# Revit family: Grinder_Pump-Zoeller-840_Series
name_source: partatom
category: Mechanical Equipment
revit_build: Autodesk Revit 2014 (Build: 20130308_1515(x64)
units: mm (PartAtom-declared; Revit-internal decimal feet)

## types (6) — shared parameters
Assembly Code = D2010900
Configuration = Reversing
Cutter & Plate SS Hardened = 55-60 Rockwell
Default Elevation = 0"
Description = Commercial Effluent Pumps
Discharge Diameter = 1.25" NPT
Discharge Radius = 5/8"
Height = 21 3/32"
Hertz = 60
Impeller Type = Ductile Iron
Installation Type = Floor Mounted
Insulation = Class F
Length = 11 19/32"
Manufacturer = Zoeller
Material = Cast Iron-Zoeller-Powder Coated Epoxy
Max. Water Temp. = 104 °F
Moisture Sensor = Moisture Sensing Probes (Requires a circuit in control panel)
Motor = 2 HP
Motor Protection = Auto Reset Thermal Overload (1 Ph), Thermal Sensor (3 Ph)
Motor Shaft = Stainless Steel
Motor Type = Submersible
Nominal Height = 5 3/8"
O-Rings = Neoprene
Operation = Non-Automatic
Overall Height = 24 7/32"
Price = Prices may vary. Please consult Manufacturer Representative for most up-to-date price list.
Product Page URL = http://www.zoellerpumps.com
RPM = 3450
Shipping Weight = 137 lbs. (1 PH), 132 lbs. (3 PH)
Tandem Seals = Mechanical Seals
Type = Capacitor Start/Capacitor Run or 3Ph.
Type SOW Power Cord Length = 240"
URL = http://www.zoellerengprod.com
Warranty Information = 36 Months (Limited)
Waste Connection = Yes
Width = 8 1/8"

## per-type parameters (varying)
| type | Apparent Load | Full Load Amps (Voltage Dependent) | Model | Phase | Voltage |
| I840-200V 1 Ph | 4000 VA | 20.0 | I840 | 1 | 200 V |
| E840-230V 1 Ph | 3956 VA | 17.2 | E840 | 1 | 230 V |
| J840-200V 3 Ph | 2460 VA | 12.3 | J840 | 3 | 200 V |
| F840-230V 3 Ph | 2484 VA | 10.8 | F840 | 3 | 230 V |
| G840-460V 3 Ph | 2530 VA | 5.5 | G840 | 3 | 460 V |
| BA840-575V 3 Ph | 2588 VA | 4.5 | BA840 | 3 | 575 V |

## geometry (parser evidence)
native form markers: Sweep x2
no freeform markers — native parametric forms only
